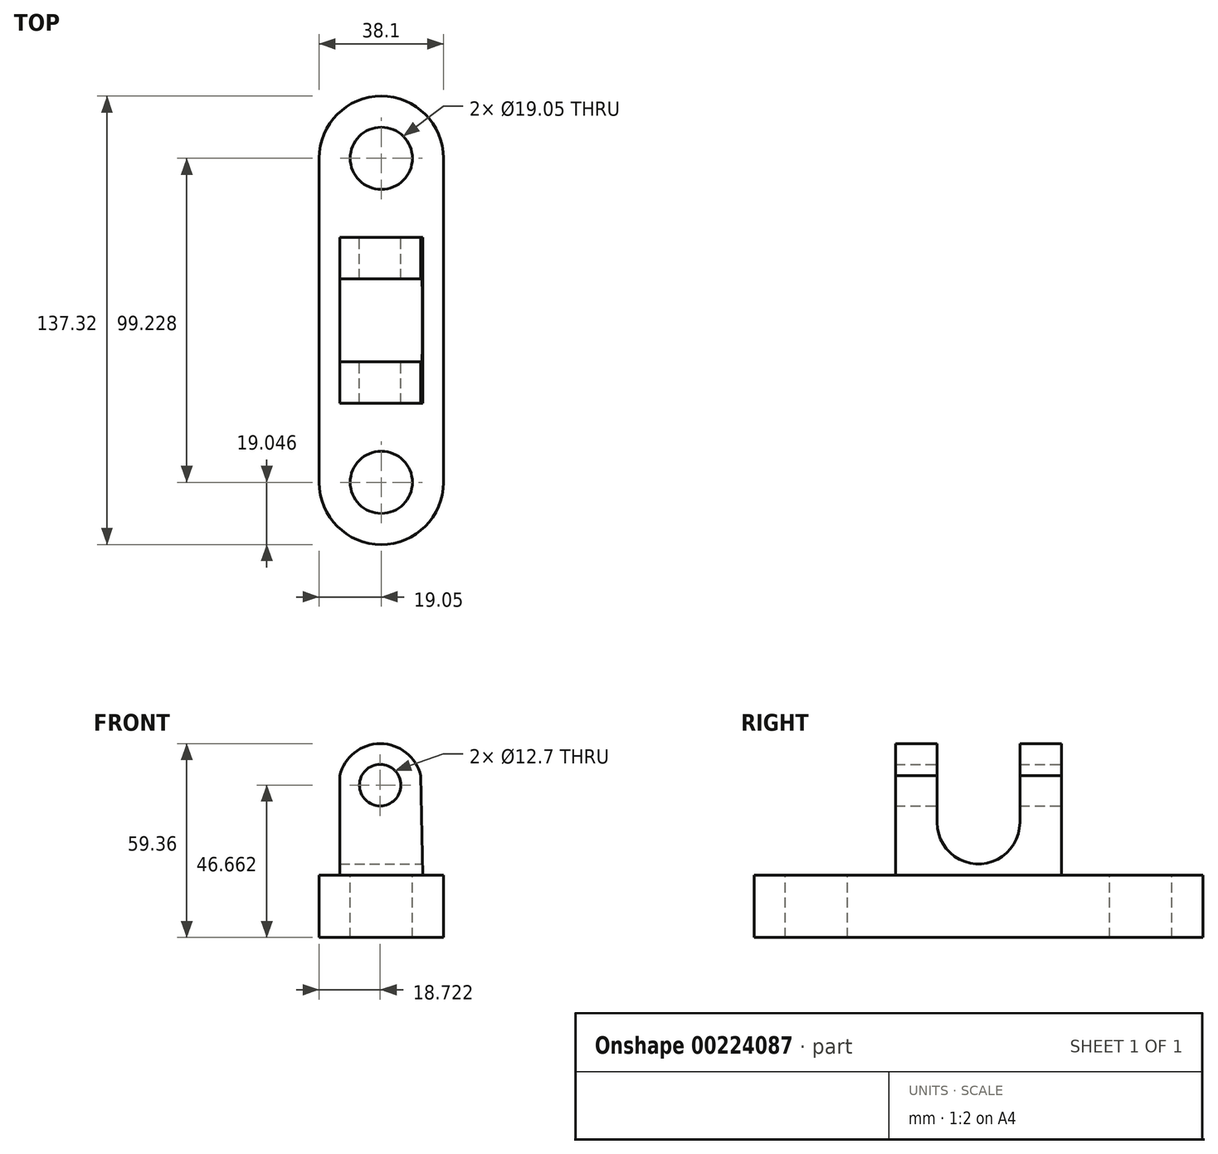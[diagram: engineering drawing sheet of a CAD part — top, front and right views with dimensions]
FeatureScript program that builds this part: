
annotation { "Feature Type Name" : "Feature", "Feature Type Description" : "" }
export const myFeature = defineFeature(function(context is Context, id is Id, definition is map)
    precondition{}
    {
        {
            var Q0;
            Q0=qCreatedBy(makeId("Top.planeOp"),FACE);
            var sketch = newSketch(context, id + "F0", { "sketchPlane" : qUnion([Q0])});
            skLineSegment(sketch, "E0.bottom", {"start": v(19.05, 49.61) * mm, "end": v(-19.05, 49.61) * mm});
            skLineSegment(sketch, "E0.top", {"start": v(19.05, -49.61) * mm, "end": v(-19.05, -49.61) * mm});
            skLineSegment(sketch, "E0.left", {"start": v(19.05, 49.61) * mm, "end": v(19.05, -49.61) * mm});
            skLineSegment(sketch, "E0.right", {"start": v(-19.05, 49.61) * mm, "end": v(-19.05, -49.61) * mm});
            skPoint(sketch, "E0.middle", {"position": v(0, 0) * mm});
            skArc(sketch, "E1", {"start": v(19.05, 49.61) * mm, "mid": v(0, 68.66) * mm, "end": v(-19.05, 49.61) * mm});
            skArc(sketch, "E2", {"start": v(-19.05, -49.61) * mm, "mid": v(0, -68.66) * mm, "end": v(19.05, -49.61) * mm});
            skSolve(sketch);
        }
        {
            var Q0;
            Q0 = qSketchRegion(id + "F0", true);
            extrude(context, id + "F1", {"entities" : qUnion([Q0]), "depth" : 19.05 * mm});
        }
        {
            var Q0;
            Q0=makeQuery(id+"F1.opExtrude","CAP_FACE",FACE,{"disambiguationData":[OSD([sQuery(id+"F0.wireOp",EDGE,"E0.left"),sQuery(id+"F0.wireOp",EDGE,"E0.right"),sQuery(id+"F0.wireOp",EDGE,"E1"),sQuery(id+"F0.wireOp",EDGE,"E2")])],"isStart":false});
            var sketch = newSketch(context, id + "F2", { "sketchPlane" : qUnion([Q0])});
            skCircle(sketch, "E3", {"center": v(0, 49.61) * mm, "radius": 9.53 * mm});
            skCircle(sketch, "E4", {"center": v(0, -49.61) * mm, "radius": 9.53 * mm});
            skSolve(sketch);
        }
        {
            var Q0;
            Q0 = qSketchRegion(id + "F2", true);
            extrude(context, id + "F3", {"entities" : qUnion([Q0]), "operationType" : NewBodyOperationType.REMOVE, "oppositeDirection" : true, "depth" : 127 * mm});
        }
        {
            var Q0;
            Q0=qCreatedBy(makeId("Front.planeOp"),FACE);
            var sketch = newSketch(context, id + "F4", { "sketchPlane" : qUnion([Q0])});
            skLineSegment(sketch, "E5", {"start": v(0, 0) * mm, "end": v(0, 19.05) * mm});
            skLineSegment(sketch, "E6", {"start": v(0, 19.05) * mm, "end": v(-12.7, 19.05) * mm});
            skLineSegment(sketch, "E7", {"start": v(0, 19.05) * mm, "end": v(12.7, 19.05) * mm});
            skLineSegment(sketch, "E8", {"start": v(-12.7, 19.05) * mm, "end": v(-12.7, 49.53) * mm});
            skLineSegment(sketch, "E9", {"start": v(12.05, 49.52) * mm, "end": v(12.7, 19.05) * mm});
            skArc(sketch, "E10", {"start": v(12.05, 49.52) * mm, "mid": v(-0.32, 59.36) * mm, "end": v(-12.7, 49.53) * mm});
            skSolve(sketch);
        }
        {
            var Q0;
            Q0 = qSketchRegion(id + "F4", true);
            extrude(context, id + "F5", {"entities" : qUnion([Q0]), "operationType" : NewBodyOperationType.ADD, "endBound" : BoundingType.SYMMETRIC, "depth" : 50.8 * mm});
        }
        {
            var Q0;
            Q0=makeQuery(id+"F5.opExtrude","CAP_FACE",FACE,{"disambiguationData":[OSD([sQuery(id+"F4.wireOp",EDGE,"E6"),sQuery(id+"F4.wireOp",EDGE,"E7"),sQuery(id+"F4.wireOp",EDGE,"E8"),sQuery(id+"F4.wireOp",EDGE,"E9"),sQuery(id+"F4.wireOp",EDGE,"E10")])],"isStart":true});
            var sketch = newSketch(context, id + "F6", { "sketchPlane" : qUnion([Q0])});
            skCircle(sketch, "E11", {"center": v(0.33, 46.66) * mm, "radius": 6.35 * mm});
            skSolve(sketch);
        }
        {
            var Q0;
            Q0 = qSketchRegion(id + "F6", true);
            extrude(context, id + "F7", {"entities" : qUnion([Q0]), "operationType" : NewBodyOperationType.REMOVE, "oppositeDirection" : true, "depth" : 127 * mm});
        }
        {
            var Q0;
            Q0=qCreatedBy(makeId("Right.planeOp"),FACE);
            var sketch = newSketch(context, id + "F8", { "sketchPlane" : qUnion([Q0])});
            skLineSegment(sketch, "E12.top", {"start": v(-12.7, 19.05) * mm, "end": v(12.7, 19.05) * mm});
            skLineSegment(sketch, "E13.top", {"start": v(12.7, 75.49) * mm, "end": v(-12.7, 75.49) * mm});
            skLineSegment(sketch, "E13.left", {"start": v(12.7, 35.17) * mm, "end": v(12.7, 75.49) * mm});
            skLineSegment(sketch, "E13.right", {"start": v(-12.7, 35.17) * mm, "end": v(-12.7, 75.49) * mm});
            skPoint(sketch, "E13.middle", {"position": v(0, 55.33) * mm});
            skArc(sketch, "E14", {"start": v(-12.7, 35.17) * mm, "mid": v(0, 22.47) * mm, "end": v(12.7, 35.17) * mm});
            skSolve(sketch);
        }
        {
            var Q0;
            Q0 = qSketchRegion(id + "F8", true);
            extrude(context, id + "F9", {"entities" : qUnion([Q0]), "operationType" : NewBodyOperationType.REMOVE, "endBound" : BoundingType.SYMMETRIC, "oppositeDirection" : true, "depth" : 127 * mm});
        }
        {
            var Q0;
            Q0 = qSketchRegion(id + "F8", true);
            extrude(context, id + "F10", {"entities" : qUnion([Q0]), "operationType" : NewBodyOperationType.REMOVE, "endBound" : BoundingType.SYMMETRIC, "oppositeDirection" : true, "depth" : 254 * mm});
        }
    });
